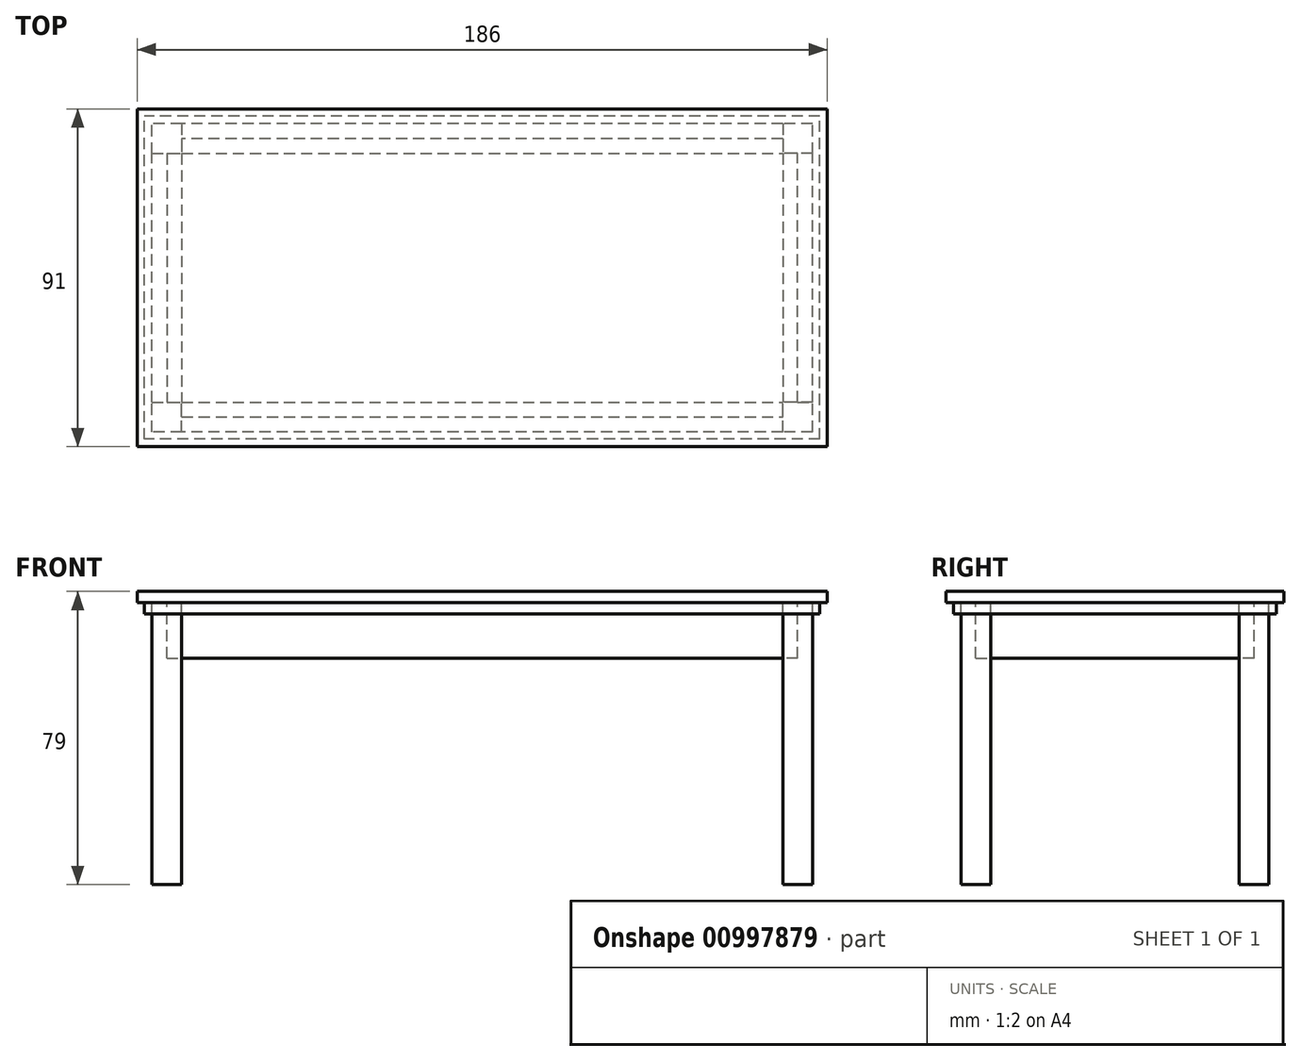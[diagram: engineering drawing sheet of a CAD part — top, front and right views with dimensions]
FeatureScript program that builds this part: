
annotation { "Feature Type Name" : "Feature", "Feature Type Description" : "" }
export const myFeature = defineFeature(function(context is Context, id is Id, definition is map)
    precondition{}
    {
        {
            var Q0;
            Q0=qCreatedBy(makeId("Top.planeOp"),FACE);
            var sketch = newSketch(context, id + "F0", { "sketchPlane" : qUnion([Q0])});
            skLineSegment(sketch, "E0.bottom", {"start": v(93, 45.5) * mm, "end": v(-93, 45.5) * mm});
            skLineSegment(sketch, "E0.top", {"start": v(93, -45.5) * mm, "end": v(-93, -45.5) * mm});
            skLineSegment(sketch, "E0.left", {"start": v(93, 45.5) * mm, "end": v(93, -45.5) * mm});
            skLineSegment(sketch, "E0.right", {"start": v(-93, 45.5) * mm, "end": v(-93, -45.5) * mm});
            skPoint(sketch, "E0.middle", {"position": v(0, 0) * mm});
            skSolve(sketch);
        }
        {
            var Q0;
            Q0 = qSketchRegion(id + "F0", true);
            extrude(context, id + "F1", {"entities" : qUnion([Q0]), "depth" : 3 * mm, "offsetDistance" : 25 * mm});
        }
        {
            var Q0;
            Q0=makeQuery(id+"F1.opExtrude","CAP_FACE",FACE,{"disambiguationData":[OSD([sQuery(id+"F0.wireOp",EDGE,"E0.bottom"),sQuery(id+"F0.wireOp",EDGE,"E0.top"),sQuery(id+"F0.wireOp",EDGE,"E0.left"),sQuery(id+"F0.wireOp",EDGE,"E0.right")])],"isStart":true});
            var sketch = newSketch(context, id + "F2", { "sketchPlane" : qUnion([Q0])});
            skLineSegment(sketch, "E1.bottom", {"start": v(91, 43.5) * mm, "end": v(-91, 43.5) * mm});
            skLineSegment(sketch, "E1.top", {"start": v(91, -43.5) * mm, "end": v(-91, -43.5) * mm});
            skLineSegment(sketch, "E1.left", {"start": v(91, 43.5) * mm, "end": v(91, -43.5) * mm});
            skLineSegment(sketch, "E1.right", {"start": v(-91, 43.5) * mm, "end": v(-91, -43.5) * mm});
            skPoint(sketch, "E1.middle", {"position": v(0, 0) * mm});
            skLineSegment(sketch, "E2.bottom", {"start": v(89, 41.5) * mm, "end": v(-89, 41.5) * mm});
            skLineSegment(sketch, "E2.top", {"start": v(89, -41.5) * mm, "end": v(-89, -41.5) * mm});
            skLineSegment(sketch, "E2.left", {"start": v(89, 41.5) * mm, "end": v(89, -41.5) * mm});
            skLineSegment(sketch, "E2.right", {"start": v(-89, 41.5) * mm, "end": v(-89, -41.5) * mm});
            skSolve(sketch);
        }
        {
            var Q0;
            Q0=makeQuery(id+"F2.imprint","IMPRINT",FACE,{"disambiguationData":[TD([[makeQuery(id+"F2.imprint","IMPRINT",EDGE,{"derivedFrom":sQuery(id+"F2.wireOp",EDGE,"E1.bottom")}),1.0]])]});
            extrude(context, id + "F3", {"entities" : qUnion([Q0]), "operationType" : NewBodyOperationType.ADD, "depth" : 3 * mm, "offsetDistance" : 25 * mm});
        }
        {
            var Q0;
            Q0=makeQuery(id+"F3.boolean.opBoolean","SPLIT",FACE,{"disambiguationData":[TD([makeQuery(id+"F3.opExtrude","SWEPT_FACE",FACE,{"disambiguationData":[OSD([sQuery(id+"F2.wireOp",EDGE,"E2.bottom")])]})])],"derivedFrom":makeQuery(id+"F1.opExtrude","CAP_FACE",FACE,{"disambiguationData":[OSD([sQuery(id+"F0.wireOp",EDGE,"E0.bottom"),sQuery(id+"F0.wireOp",EDGE,"E0.top"),sQuery(id+"F0.wireOp",EDGE,"E0.left"),sQuery(id+"F0.wireOp",EDGE,"E0.right")])],"isStart":true})});
            var sketch = newSketch(context, id + "F4", { "sketchPlane" : qUnion([Q0])});
            skLineSegment(sketch, "E3.bottom", {"start": v(-89, 41.5) * mm, "end": v(-81, 41.5) * mm});
            skLineSegment(sketch, "E3.top", {"start": v(-89, 33.5) * mm, "end": v(-81, 33.5) * mm});
            skLineSegment(sketch, "E3.left", {"start": v(-89, 41.5) * mm, "end": v(-89, 33.5) * mm});
            skLineSegment(sketch, "E3.right", {"start": v(-81, 41.5) * mm, "end": v(-81, 33.5) * mm});
            skLineSegment(sketch, "E4.bottom", {"start": v(89, 41.5) * mm, "end": v(81, 41.5) * mm});
            skLineSegment(sketch, "E4.top", {"start": v(89, 33.5) * mm, "end": v(81, 33.5) * mm});
            skLineSegment(sketch, "E4.left", {"start": v(89, 41.5) * mm, "end": v(89, 33.5) * mm});
            skLineSegment(sketch, "E4.right", {"start": v(81, 41.5) * mm, "end": v(81, 33.5) * mm});
            skLineSegment(sketch, "E5.bottom", {"start": v(89, -41.5) * mm, "end": v(81, -41.5) * mm});
            skLineSegment(sketch, "E5.top", {"start": v(89, -33.5) * mm, "end": v(81, -33.5) * mm});
            skLineSegment(sketch, "E5.left", {"start": v(89, -41.5) * mm, "end": v(89, -33.5) * mm});
            skLineSegment(sketch, "E5.right", {"start": v(81, -41.5) * mm, "end": v(81, -33.5) * mm});
            skLineSegment(sketch, "E6.bottom", {"start": v(-89, -41.5) * mm, "end": v(-81, -41.5) * mm});
            skLineSegment(sketch, "E6.top", {"start": v(-89, -33.5) * mm, "end": v(-81, -33.5) * mm});
            skLineSegment(sketch, "E6.left", {"start": v(-89, -41.5) * mm, "end": v(-89, -33.5) * mm});
            skLineSegment(sketch, "E6.right", {"start": v(-81, -41.5) * mm, "end": v(-81, -33.5) * mm});
            skSolve(sketch);
        }
        {
            var Q0;
            Q0=makeQuery(id+"F4.imprint","IMPRINT",FACE,{"disambiguationData":[TD([[makeQuery(id+"F4.imprint","IMPRINT",EDGE,{"derivedFrom":sQuery(id+"F4.wireOp",EDGE,"E3.bottom")}),1.0]])]});
            var Q1;
            Q1=makeQuery(id+"F4.imprint","IMPRINT",FACE,{"disambiguationData":[TD([[makeQuery(id+"F4.imprint","IMPRINT",EDGE,{"derivedFrom":sQuery(id+"F4.wireOp",EDGE,"E6.bottom")}),-1.0]])]});
            var Q2;
            Q2=makeQuery(id+"F4.imprint","IMPRINT",FACE,{"disambiguationData":[TD([[makeQuery(id+"F4.imprint","IMPRINT",EDGE,{"derivedFrom":sQuery(id+"F4.wireOp",EDGE,"E4.bottom")}),1.0]])]});
            var Q3;
            Q3=makeQuery(id+"F4.imprint","IMPRINT",FACE,{"disambiguationData":[TD([[makeQuery(id+"F4.imprint","IMPRINT",EDGE,{"derivedFrom":sQuery(id+"F4.wireOp",EDGE,"E5.bottom")}),-1.0]])]});
            extrude(context, id + "F5", {"entities" : qUnion([Q0, Q1, Q2, Q3]), "operationType" : NewBodyOperationType.ADD, "depth" : 76 * mm, "offsetDistance" : 25 * mm});
        }
        {
            var Q0;
            Q0=makeQuery(id+"F3.boolean.opBoolean","SPLIT",FACE,{"disambiguationData":[TD([makeQuery(id+"F3.opExtrude","SWEPT_FACE",FACE,{"disambiguationData":[OSD([sQuery(id+"F2.wireOp",EDGE,"E2.bottom")])]})])],"derivedFrom":makeQuery(id+"F1.opExtrude","CAP_FACE",FACE,{"disambiguationData":[OSD([sQuery(id+"F0.wireOp",EDGE,"E0.bottom"),sQuery(id+"F0.wireOp",EDGE,"E0.top"),sQuery(id+"F0.wireOp",EDGE,"E0.left"),sQuery(id+"F0.wireOp",EDGE,"E0.right")])],"isStart":true})});
            var sketch = newSketch(context, id + "F6", { "sketchPlane" : qUnion([Q0])});
            skLineSegment(sketch, "E7.bottom", {"start": v(-81, 37.5) * mm, "end": v(81, 37.5) * mm});
            skLineSegment(sketch, "E7.top", {"start": v(-81, 33.5) * mm, "end": v(81, 33.5) * mm});
            skLineSegment(sketch, "E7.left", {"start": v(-81, 37.5) * mm, "end": v(-81, 33.5) * mm});
            skLineSegment(sketch, "E7.right", {"start": v(81, 37.5) * mm, "end": v(81, 33.5) * mm});
            skLineSegment(sketch, "E8.bottom", {"start": v(85, 33.5) * mm, "end": v(81, 33.5) * mm});
            skLineSegment(sketch, "E8.top", {"start": v(85, -33.5) * mm, "end": v(81, -33.5) * mm});
            skLineSegment(sketch, "E8.left", {"start": v(85, 33.5) * mm, "end": v(85, -33.5) * mm});
            skLineSegment(sketch, "E8.right", {"start": v(81, 33.5) * mm, "end": v(81, -33.5) * mm});
            skLineSegment(sketch, "E9.bottom", {"start": v(81, -37.5) * mm, "end": v(-81, -37.5) * mm});
            skLineSegment(sketch, "E9.top", {"start": v(81, -33.5) * mm, "end": v(-81, -33.5) * mm});
            skLineSegment(sketch, "E9.left", {"start": v(81, -37.5) * mm, "end": v(81, -33.5) * mm});
            skLineSegment(sketch, "E9.right", {"start": v(-81, -37.5) * mm, "end": v(-81, -33.5) * mm});
            skLineSegment(sketch, "E10.bottom", {"start": v(-85, -33.5) * mm, "end": v(-81, -33.5) * mm});
            skLineSegment(sketch, "E10.top", {"start": v(-85, 33.5) * mm, "end": v(-81, 33.5) * mm});
            skLineSegment(sketch, "E10.left", {"start": v(-85, -33.5) * mm, "end": v(-85, 33.5) * mm});
            skLineSegment(sketch, "E10.right", {"start": v(-81, -33.5) * mm, "end": v(-81, 33.5) * mm});
            skSolve(sketch);
        }
        {
            var Q0;
            Q0=makeQuery(id+"F6.imprint","IMPRINT",FACE,{"disambiguationData":[TD([[makeQuery(id+"F6.imprint","IMPRINT",EDGE,{"derivedFrom":sQuery(id+"F6.wireOp",EDGE,"E8.bottom")}),1.0]])]});
            var Q1;
            Q1=makeQuery(id+"F6.imprint","IMPRINT",FACE,{"disambiguationData":[TD([[makeQuery(id+"F6.imprint","IMPRINT",EDGE,{"derivedFrom":sQuery(id+"F6.wireOp",EDGE,"E9.bottom")}),-1.0]])]});
            var Q2;
            Q2=makeQuery(id+"F6.imprint","IMPRINT",FACE,{"disambiguationData":[TD([[makeQuery(id+"F6.imprint","IMPRINT",EDGE,{"derivedFrom":sQuery(id+"F6.wireOp",EDGE,"E10.bottom")}),1.0]])]});
            var Q3;
            Q3=makeQuery(id+"F6.imprint","IMPRINT",FACE,{"disambiguationData":[TD([[makeQuery(id+"F6.imprint","IMPRINT",EDGE,{"derivedFrom":sQuery(id+"F6.wireOp",EDGE,"E7.bottom")}),-1.0]])]});
            extrude(context, id + "F7", {"entities" : qUnion([Q0, Q1, Q2, Q3]), "operationType" : NewBodyOperationType.ADD, "depth" : 15 * mm, "offsetDistance" : 25 * mm});
        }
    });
